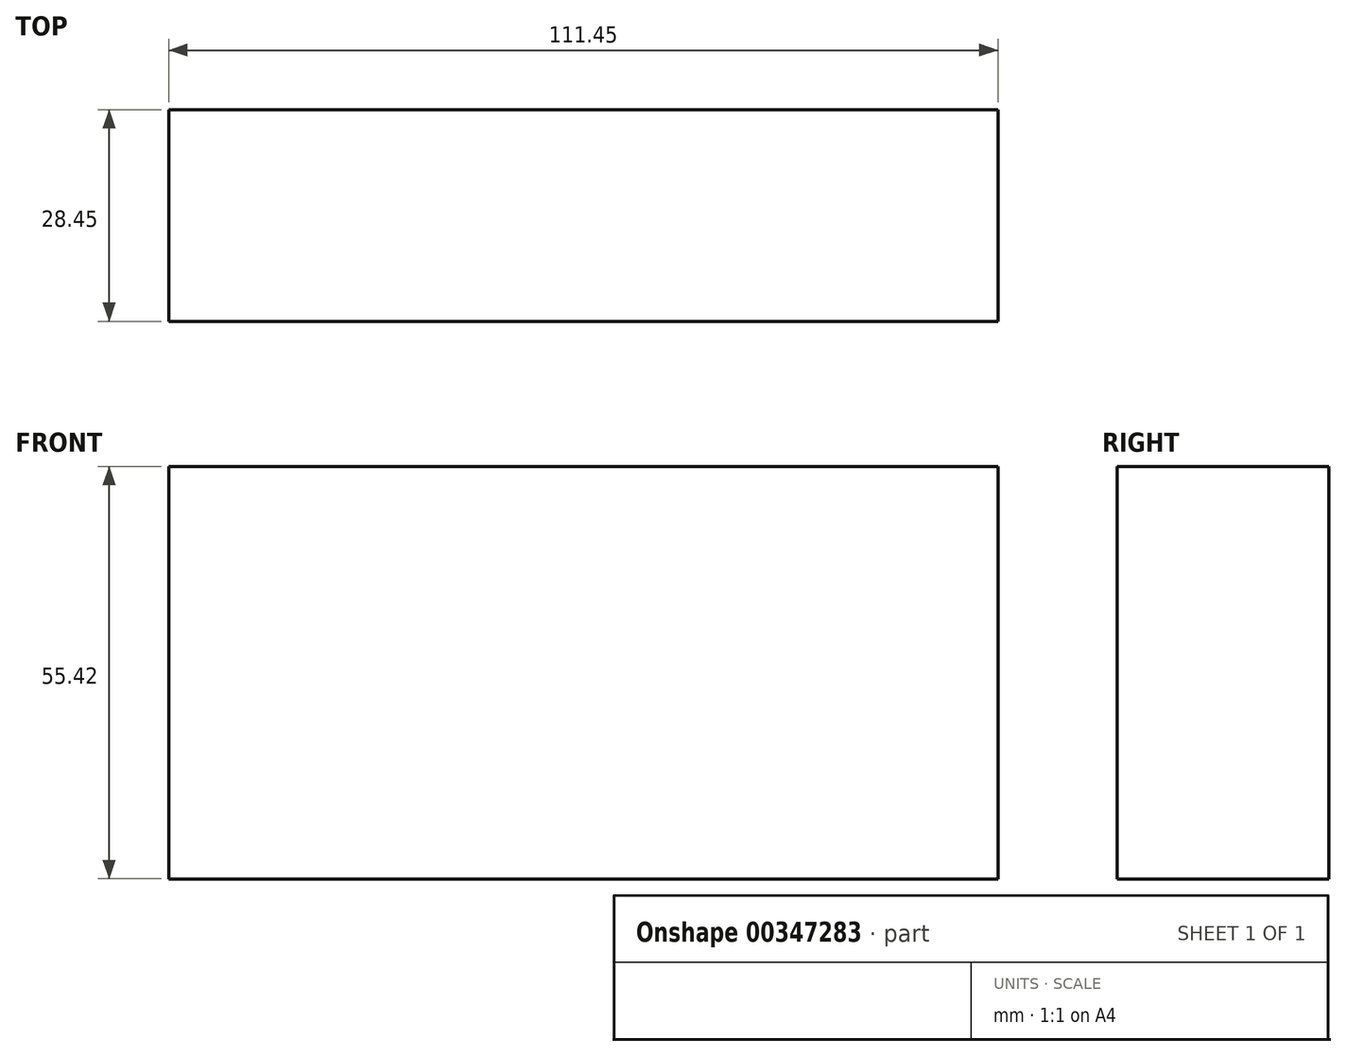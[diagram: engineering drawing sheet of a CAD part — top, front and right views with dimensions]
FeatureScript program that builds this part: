
annotation { "Feature Type Name" : "Feature", "Feature Type Description" : "" }
export const myFeature = defineFeature(function(context is Context, id is Id, definition is map)
    precondition{}
    {
        {
            var Q0;
            Q0=qCreatedBy(makeId("Front.planeOp"),FACE);
            var sketch = newSketch(context, id + "F0", { "sketchPlane" : qUnion([Q0])});
            skLineSegment(sketch, "E0.bottom", {"start": v(-49.33, 32.89) * mm, "end": v(62.12, 32.89) * mm});
            skLineSegment(sketch, "E0.top", {"start": v(-49.33, -22.53) * mm, "end": v(62.12, -22.53) * mm});
            skLineSegment(sketch, "E0.left", {"start": v(-49.33, 32.89) * mm, "end": v(-49.33, -22.53) * mm});
            skLineSegment(sketch, "E0.right", {"start": v(62.12, 32.89) * mm, "end": v(62.12, -22.53) * mm});
            skSolve(sketch);
        }
        {
            var Q0;
            Q0=makeQuery(id+"F0.imprint","IMPRINT",FACE,{"disambiguationData":[TD([[makeQuery(id+"F0.imprint","IMPRINT",EDGE,{"derivedFrom":sQuery(id+"F0.wireOp",EDGE,"E0.bottom")}),-1.0]])]});
            extrude(context, id + "F1", {"entities" : qUnion([Q0]), "oppositeDirection" : true, "depth" : 3.05 * mm});
        }
        {
            var Q0;
            Q0=makeQuery(id+"F0.imprint","IMPRINT",FACE,{"disambiguationData":[TD([[makeQuery(id+"F0.imprint","IMPRINT",EDGE,{"derivedFrom":sQuery(id+"F0.wireOp",EDGE,"E0.bottom")}),-1.0]])]});
            extrude(context, id + "F2", {"entities" : qUnion([Q0]), "operationType" : NewBodyOperationType.ADD, "depth" : 25.4 * mm});
        }
    });
